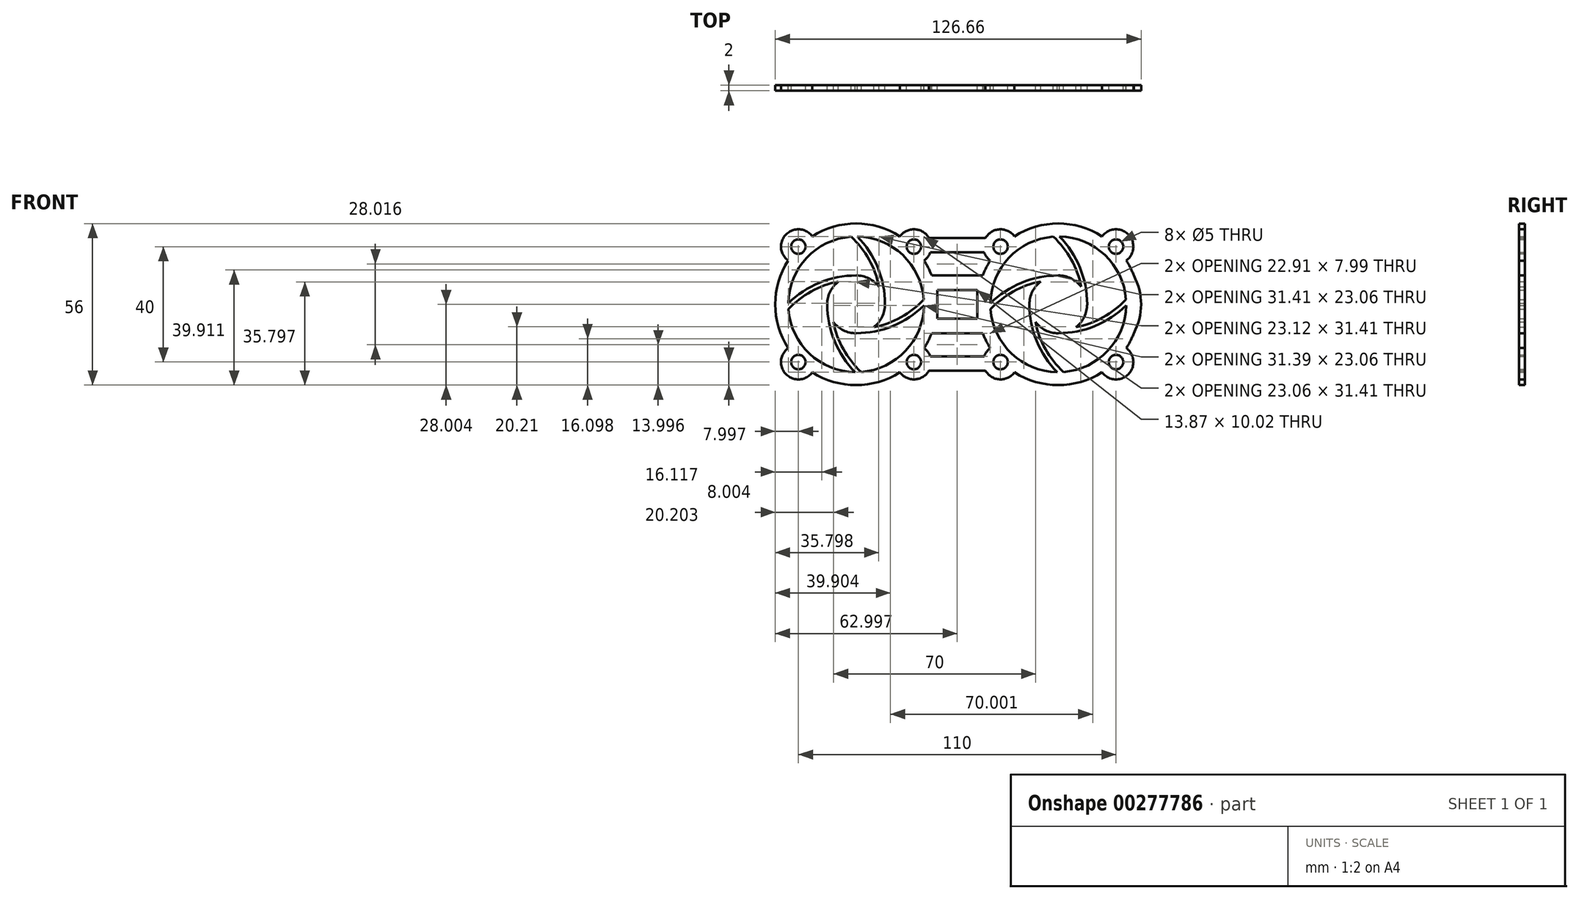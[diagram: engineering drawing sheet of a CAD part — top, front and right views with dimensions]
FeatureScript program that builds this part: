
annotation { "Feature Type Name" : "Feature", "Feature Type Description" : "" }
export const myFeature = defineFeature(function(context is Context, id is Id, definition is map)
    precondition{}
    {
        {
            var Q0;
            Q0=qCreatedBy(makeId("Front.planeOp"),FACE);
            var sketch = newSketch(context, id + "F0", { "sketchPlane" : qUnion([Q0])});
            skArc(sketch, "E0", {"start": v(11.47, 23.38) * mm, "mid": v(-3.9, 16.08) * mm, "end": v(-10.32, 0.32) * mm});
            skArc(sketch, "E1.0", {"start": v(28.33, 23.49) * mm, "mid": v(13.18, 27.94) * mm, "end": v(-1.98, 23.49) * mm});
            skCircle(sketch, "E2", {"center": v(-6.82, 19.94) * mm, "radius": 2.5 * mm});
            skCircle(sketch, "E3", {"center": v(33.18, 19.94) * mm, "radius": 2.5 * mm});
            skCircle(sketch, "E4", {"center": v(33.18, -20.06) * mm, "radius": 2.5 * mm});
            skCircle(sketch, "E5", {"center": v(-6.82, -20.06) * mm, "radius": 2.5 * mm});
            skArc(sketch, "E6.0", {"start": v(36.72, 15.1) * mm, "mid": v(37.42, 24.19) * mm, "end": v(28.33, 23.49) * mm});
            skArc(sketch, "E7.0", {"start": v(-1.98, 23.49) * mm, "mid": v(-7.14, 25.94) * mm, "end": v(-12.02, 22.95) * mm});
            skArc(sketch, "E8.0", {"start": v(-10.37, -15.21) * mm, "mid": v(-11.64, -16.48) * mm, "end": v(-12.48, -18.06) * mm});
            skArc(sketch, "E9.0", {"start": v(28.33, -23.6) * mm, "mid": v(37.42, -24.3) * mm, "end": v(36.72, -15.21) * mm});
            skArc(sketch, "E10", {"start": v(-58.54, 23.38) * mm, "mid": v(-73.9, 16.08) * mm, "end": v(-80.32, 0.32) * mm});
            skArc(sketch, "E11.0", {"start": v(-30.67, 9.96) * mm, "mid": v(-31.84, 12.6) * mm, "end": v(-33.28, 15.1) * mm});
            skCircle(sketch, "E12", {"center": v(-76.82, 19.94) * mm, "radius": 2.5 * mm});
            skCircle(sketch, "E13", {"center": v(-36.82, 19.94) * mm, "radius": 2.5 * mm});
            skCircle(sketch, "E14", {"center": v(-36.82, -20.06) * mm, "radius": 2.5 * mm});
            skCircle(sketch, "E15", {"center": v(-76.82, -20.06) * mm, "radius": 2.5 * mm});
            skArc(sketch, "E16.0", {"start": v(-31.63, 22.95) * mm, "mid": v(-36.5, 25.94) * mm, "end": v(-41.67, 23.49) * mm});
            skArc(sketch, "E17.0", {"start": v(-71.98, 23.49) * mm, "mid": v(-81.07, 24.19) * mm, "end": v(-80.37, 15.1) * mm});
            skArc(sketch, "E18.0", {"start": v(-80.37, -15.21) * mm, "mid": v(-81.07, -24.3) * mm, "end": v(-71.98, -23.6) * mm});
            skArc(sketch, "E19.0", {"start": v(-31.16, -18.06) * mm, "mid": v(-32, -16.48) * mm, "end": v(-33.28, -15.21) * mm});
            skLineSegment(sketch, "E20", {"start": v(-56.82, -32.43) * mm, "end": v(-56.82, -0.06) * mm, "construction": true});
            skLineSegment(sketch, "E21", {"start": v(-56.82, -0.06) * mm, "end": v(-105.9, -0.06) * mm, "construction": true});
            skLineSegment(sketch, "E22", {"start": v(-31.63, 22.95) * mm, "end": v(-12.02, 22.95) * mm});
            skLineSegment(sketch, "E23.0", {"start": v(-31.16, 17.95) * mm, "end": v(-12.48, 17.95) * mm});
            skLineSegment(sketch, "E24", {"start": v(-30.67, 9.96) * mm, "end": v(-12.97, 9.96) * mm});
            skLineSegment(sketch, "E25.0", {"start": v(-28.76, 4.96) * mm, "end": v(-14.89, 4.96) * mm});
            skLineSegment(sketch, "E26.MirrorCS", {"start": v(-28.76, -5.07) * mm, "end": v(-14.89, -5.07) * mm});
            skLineSegment(sketch, "E27.MirrorCS", {"start": v(-30.67, -10.07) * mm, "end": v(-12.97, -10.07) * mm});
            skLineSegment(sketch, "E28.MirrorCS", {"start": v(-31.63, -23.06) * mm, "end": v(-12.02, -23.06) * mm});
            skLineSegment(sketch, "E29.MirrorCS", {"start": v(-31.16, -18.06) * mm, "end": v(-12.48, -18.06) * mm});
            skLineSegment(sketch, "E30.top", {"start": v(39.33, -10.04) * mm, "end": v(39.34, -10.04) * mm});
            skArc(sketch, "E31.trimOffspring", {"start": v(-10.37, 15.1) * mm, "mid": v(-11.8, 12.6) * mm, "end": v(-12.97, 9.96) * mm});
            skArc(sketch, "E32.trimOffspring", {"start": v(36.72, -15.21) * mm, "mid": v(38.16, -12.7) * mm, "end": v(39.34, -10.04) * mm});
            skArc(sketch, "E33.trimOffspring", {"start": v(-1.98, -23.6) * mm, "mid": v(13.18, -28.06) * mm, "end": v(28.33, -23.6) * mm});
            skPoint(sketch, "E34.orphan", {"position": v(-12.02, -18.06) * mm});
            skArc(sketch, "E35.trimOffspring", {"start": v(-12.02, -23.06) * mm, "mid": v(-7.14, -26.05) * mm, "end": v(-1.98, -23.6) * mm});
            skPoint(sketch, "E36.orphan", {"position": v(-12.02, 17.95) * mm});
            skArc(sketch, "E37.trimOffspring", {"start": v(-12.48, 17.95) * mm, "mid": v(-11.64, 16.36) * mm, "end": v(-10.37, 15.1) * mm});
            skLineSegment(sketch, "E38", {"start": v(-14.89, 4.96) * mm, "end": v(-14.89, -5.07) * mm});
            skLineSegment(sketch, "E39", {"start": v(-28.76, 4.96) * mm, "end": v(-28.76, -5.07) * mm});
            skPoint(sketch, "E40.orphan", {"position": v(-12.97, 4.96) * mm});
            skArc(sketch, "E41.trimOffspring", {"start": v(-12.97, -10.07) * mm, "mid": v(-11.8, -12.7) * mm, "end": v(-10.37, -15.21) * mm});
            skPoint(sketch, "E42.orphan", {"position": v(-30.67, 4.96) * mm});
            skPoint(sketch, "E43.orphan", {"position": v(-12.97, -5.07) * mm});
            skPoint(sketch, "E44.orphan", {"position": v(-30.67, -5.07) * mm});
            skPoint(sketch, "E45.orphan", {"position": v(-31.63, 17.95) * mm});
            skPoint(sketch, "E46.orphan", {"position": v(-31.63, -18.06) * mm});
            skArc(sketch, "E47.trimOffspring", {"start": v(-41.67, 23.49) * mm, "mid": v(-56.82, 27.94) * mm, "end": v(-71.98, 23.49) * mm});
            skArc(sketch, "E48.trimOffspring", {"start": v(-33.28, 15.1) * mm, "mid": v(-32, 16.36) * mm, "end": v(-31.16, 17.95) * mm});
            skArc(sketch, "E49.trimOffspring", {"start": v(-80.37, 15.1) * mm, "mid": v(-84.82, -0.06) * mm, "end": v(-80.37, -15.21) * mm});
            skArc(sketch, "E50.trimOffspring", {"start": v(-71.98, -23.6) * mm, "mid": v(-56.82, -28.06) * mm, "end": v(-41.67, -23.6) * mm});
            skArc(sketch, "E51.trimOffspring", {"start": v(-33.28, -15.21) * mm, "mid": v(-31.84, -12.7) * mm, "end": v(-30.67, -10.07) * mm});
            skArc(sketch, "E52.trimOffspring", {"start": v(-41.67, -23.6) * mm, "mid": v(-36.5, -26.05) * mm, "end": v(-31.63, -23.06) * mm});
            skLineSegment(sketch, "E53", {"start": v(41.24, 4.94) * mm, "end": v(41.24, 4.93) * mm});
            skArc(sketch, "E54.trimOffspring", {"start": v(39.33, 9.94) * mm, "mid": v(38.16, 12.59) * mm, "end": v(36.72, 15.1) * mm});
            skLineSegment(sketch, "E55", {"start": v(-56.82, -0.06) * mm, "end": v(-56.82, 39.8) * mm, "construction": true});
            skArc(sketch, "E56", {"start": v(39.34, -10.04) * mm, "mid": v(41.84, -0.05) * mm, "end": v(39.33, 9.94) * mm});
            skLineSegment(sketch, "E57", {"start": v(13.18, -0.06) * mm, "end": v(13.18, 39.7) * mm, "construction": true});
            skPoint(sketch, "E57.endSnap0", {"position": v(13.18, 27.94) * mm});
            skLineSegment(sketch, "E58", {"start": v(13.18, -0.06) * mm, "end": v(13.18, -38) * mm, "construction": true});
            skArc(sketch, "E59", {"start": v(-48.91, 6.06) * mm, "mid": v(-52.42, 8.92) * mm, "end": v(-56.82, 9.94) * mm});
            skArc(sketch, "E60", {"start": v(21.09, 6.06) * mm, "mid": v(17.58, 8.92) * mm, "end": v(13.18, 9.94) * mm});
            skArc(sketch, "E61", {"start": v(-46.82, -0.06) * mm, "mid": v(-49.32, 12.64) * mm, "end": v(-56.45, 23.44) * mm});
            skArc(sketch, "E62", {"start": v(-56.82, 9.94) * mm, "mid": v(-69.52, 7.45) * mm, "end": v(-80.32, 0.32) * mm});
            skArc(sketch, "E63", {"start": v(-66.82, -0.06) * mm, "mid": v(-64.3, -12.76) * mm, "end": v(-57.14, -23.55) * mm});
            skArc(sketch, "E64", {"start": v(-56.82, -10.06) * mm, "mid": v(-44.13, -7.56) * mm, "end": v(-33.33, -0.43) * mm});
            skArc(sketch, "E65", {"start": v(23.18, -0.05) * mm, "mid": v(20.68, 12.64) * mm, "end": v(13.56, 23.44) * mm});
            skArc(sketch, "E66", {"start": v(13.18, 9.94) * mm, "mid": v(0.48, 7.45) * mm, "end": v(-10.32, 0.32) * mm});
            skPoint(sketch, "E66.startSnap0", {"position": v(13.18, -19.03) * mm});
            skArc(sketch, "E67", {"start": v(3.18, -0.05) * mm, "mid": v(5.7, -12.76) * mm, "end": v(12.86, -23.55) * mm});
            skArc(sketch, "E68", {"start": v(13.18, -10.06) * mm, "mid": v(25.87, -7.56) * mm, "end": v(36.67, -0.43) * mm});
            skArc(sketch, "E69.0", {"start": v(-48.91, 6.06) * mm, "mid": v(-52.35, 15.49) * mm, "end": v(-58.54, 23.38) * mm});
            skArc(sketch, "E70.0", {"start": v(-62.94, 7.85) * mm, "mid": v(-72.36, 4.42) * mm, "end": v(-80.26, -1.77) * mm});
            skArc(sketch, "E71.0", {"start": v(-65.32, -0.05) * mm, "mid": v(-65.32, -0.05) * mm, "end": v(-65.32, -0.06) * mm});
            skArc(sketch, "E72.0", {"start": v(-50.7, -7.97) * mm, "mid": v(-41.28, -4.53) * mm, "end": v(-33.39, 1.66) * mm});
            skArc(sketch, "E73.0", {"start": v(7.06, 7.85) * mm, "mid": v(-2.36, 4.42) * mm, "end": v(-10.26, -1.77) * mm});
            skArc(sketch, "E74.0", {"start": v(5.28, -6.2) * mm, "mid": v(8.74, -15.6) * mm, "end": v(14.95, -23.49) * mm});
            skArc(sketch, "E75.0", {"start": v(19.3, -7.97) * mm, "mid": v(28.72, -4.53) * mm, "end": v(36.61, 1.66) * mm});
            skArc(sketch, "E76.0", {"start": v(21.09, 6.06) * mm, "mid": v(17.65, 15.49) * mm, "end": v(11.47, 23.38) * mm});
            skArc(sketch, "E77.trimOffspring", {"start": v(-64.72, -6.2) * mm, "mid": v(-61.26, -15.6) * mm, "end": v(-55.05, -23.49) * mm});
            skArc(sketch, "E78.trimOffspring", {"start": v(-62.94, 7.85) * mm, "mid": v(-65.81, 4.33) * mm, "end": v(-66.82, -0.1) * mm});
            skArc(sketch, "E79.trimOffspring", {"start": v(-64.72, -6.2) * mm, "mid": v(-61.22, -9.04) * mm, "end": v(-56.82, -10.06) * mm});
            skArc(sketch, "E80.trimOffspring", {"start": v(-50.7, -7.97) * mm, "mid": v(-47.85, -4.46) * mm, "end": v(-46.82, -0.06) * mm});
            skArc(sketch, "E81.trimOffspring", {"start": v(-80.26, -1.77) * mm, "mid": v(-72.94, -17.16) * mm, "end": v(-57.14, -23.55) * mm});
            skPoint(sketch, "E82.trimOffspring.end.orphan", {"position": v(-54.06, -26.3) * mm});
            skArc(sketch, "E83.trimOffspring", {"start": v(-55.05, -23.49) * mm, "mid": v(-39.72, -16.17) * mm, "end": v(-33.33, -0.43) * mm});
            skArc(sketch, "E84.trimOffspring", {"start": v(-33.39, 1.66) * mm, "mid": v(-40.69, 17.03) * mm, "end": v(-56.45, 23.44) * mm});
            skArc(sketch, "E85.trimOffspring", {"start": v(7.06, 7.85) * mm, "mid": v(4.19, 4.33) * mm, "end": v(3.18, -0.1) * mm});
            skArc(sketch, "E86.trimOffspring", {"start": v(5.28, -6.2) * mm, "mid": v(8.78, -9.04) * mm, "end": v(13.18, -10.06) * mm});
            skArc(sketch, "E87.trimOffspring", {"start": v(19.3, -7.97) * mm, "mid": v(22.15, -4.46) * mm, "end": v(23.18, -0.05) * mm});
            skArc(sketch, "E88.trimOffspring", {"start": v(-10.26, -1.77) * mm, "mid": v(-2.94, -17.16) * mm, "end": v(12.86, -23.55) * mm});
            skPoint(sketch, "E89.orphan", {"position": v(15.94, -26.3) * mm});
            skArc(sketch, "E90.trimOffspring", {"start": v(14.95, -23.49) * mm, "mid": v(30.28, -16.17) * mm, "end": v(36.67, -0.43) * mm});
            skArc(sketch, "E91.trimOffspring", {"start": v(36.61, 1.66) * mm, "mid": v(29.31, 17.03) * mm, "end": v(13.56, 23.44) * mm});
            skSolve(sketch);
        }
        {
            var Q0;
            Q0 = qSketchRegion(id + "F0", true);
            extrude(context, id + "F1", {"entities" : qUnion([Q0]), "depth" : 2 * mm});
        }
        {
            var Q0;
            Q0=makeQuery(id+"F1.opExtrude","SWEPT_BODY",BODY,{"disambiguationData":[OSD([sQuery(id+"F0.wireOp",EDGE,"E0"),sQuery(id+"F0.wireOp",EDGE,"E1.0"),sQuery(id+"F0.wireOp",EDGE,"E2"),sQuery(id+"F0.wireOp",EDGE,"E3"),sQuery(id+"F0.wireOp",EDGE,"E4"),sQuery(id+"F0.wireOp",EDGE,"E5"),sQuery(id+"F0.wireOp",EDGE,"E6.0"),sQuery(id+"F0.wireOp",EDGE,"E7.0"),sQuery(id+"F0.wireOp",EDGE,"E8.0"),sQuery(id+"F0.wireOp",EDGE,"E9.0"),sQuery(id+"F0.wireOp",EDGE,"E10"),sQuery(id+"F0.wireOp",EDGE,"E11.0"),sQuery(id+"F0.wireOp",EDGE,"E12"),sQuery(id+"F0.wireOp",EDGE,"E13"),sQuery(id+"F0.wireOp",EDGE,"E14"),sQuery(id+"F0.wireOp",EDGE,"E15"),sQuery(id+"F0.wireOp",EDGE,"E16.0"),sQuery(id+"F0.wireOp",EDGE,"E17.0"),sQuery(id+"F0.wireOp",EDGE,"E18.0"),sQuery(id+"F0.wireOp",EDGE,"E19.0"),sQuery(id+"F0.wireOp",EDGE,"E22"),sQuery(id+"F0.wireOp",EDGE,"E23.0"),sQuery(id+"F0.wireOp",EDGE,"E24"),sQuery(id+"F0.wireOp",EDGE,"E25.0"),sQuery(id+"F0.wireOp",EDGE,"E26.MirrorCS"),sQuery(id+"F0.wireOp",EDGE,"E27.MirrorCS"),sQuery(id+"F0.wireOp",EDGE,"E28.MirrorCS"),sQuery(id+"F0.wireOp",EDGE,"E29.MirrorCS"),sQuery(id+"F0.wireOp",EDGE,"E31.trimOffspring"),sQuery(id+"F0.wireOp",EDGE,"E32.trimOffspring"),sQuery(id+"F0.wireOp",EDGE,"E33.trimOffspring"),sQuery(id+"F0.wireOp",EDGE,"E35.trimOffspring"),sQuery(id+"F0.wireOp",EDGE,"E37.trimOffspring"),sQuery(id+"F0.wireOp",EDGE,"E38"),sQuery(id+"F0.wireOp",EDGE,"E39"),sQuery(id+"F0.wireOp",EDGE,"E41.trimOffspring"),sQuery(id+"F0.wireOp",EDGE,"E47.trimOffspring"),sQuery(id+"F0.wireOp",EDGE,"E48.trimOffspring"),sQuery(id+"F0.wireOp",EDGE,"E49.trimOffspring"),sQuery(id+"F0.wireOp",EDGE,"E50.trimOffspring"),sQuery(id+"F0.wireOp",EDGE,"E51.trimOffspring"),sQuery(id+"F0.wireOp",EDGE,"E52.trimOffspring"),sQuery(id+"F0.wireOp",EDGE,"E54.trimOffspring"),sQuery(id+"F0.wireOp",EDGE,"E56"),sQuery(id+"F0.wireOp",EDGE,"E59"),sQuery(id+"F0.wireOp",EDGE,"E60"),sQuery(id+"F0.wireOp",EDGE,"E61"),sQuery(id+"F0.wireOp",EDGE,"E62"),sQuery(id+"F0.wireOp",EDGE,"E63"),sQuery(id+"F0.wireOp",EDGE,"E64"),sQuery(id+"F0.wireOp",EDGE,"E65"),sQuery(id+"F0.wireOp",EDGE,"E66"),sQuery(id+"F0.wireOp",EDGE,"E67"),sQuery(id+"F0.wireOp",EDGE,"E68"),sQuery(id+"F0.wireOp",EDGE,"E69.0"),sQuery(id+"F0.wireOp",EDGE,"E70.0"),sQuery(id+"F0.wireOp",EDGE,"E72.0"),sQuery(id+"F0.wireOp",EDGE,"E73.0"),sQuery(id+"F0.wireOp",EDGE,"E74.0"),sQuery(id+"F0.wireOp",EDGE,"E75.0"),sQuery(id+"F0.wireOp",EDGE,"E76.0"),sQuery(id+"F0.wireOp",EDGE,"E77.trimOffspring"),sQuery(id+"F0.wireOp",EDGE,"E78.trimOffspring"),sQuery(id+"F0.wireOp",EDGE,"E79.trimOffspring"),sQuery(id+"F0.wireOp",EDGE,"E80.trimOffspring"),sQuery(id+"F0.wireOp",EDGE,"E81.trimOffspring"),sQuery(id+"F0.wireOp",EDGE,"E83.trimOffspring"),sQuery(id+"F0.wireOp",EDGE,"E84.trimOffspring"),sQuery(id+"F0.wireOp",EDGE,"E85.trimOffspring"),sQuery(id+"F0.wireOp",EDGE,"E86.trimOffspring"),sQuery(id+"F0.wireOp",EDGE,"E87.trimOffspring"),sQuery(id+"F0.wireOp",EDGE,"E88.trimOffspring"),sQuery(id+"F0.wireOp",EDGE,"E90.trimOffspring"),sQuery(id+"F0.wireOp",EDGE,"E91.trimOffspring")])]});
            transform(context, id + "F2", {"entities" : qUnion([Q0]), "transformType" : TransformType.TRANSLATION_3D, "dx" : 21.6 * mm, "dy" : 0 * mm, "dz" : 0 * mm, "makeCopy" : false});
        }
    });
